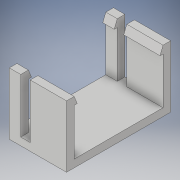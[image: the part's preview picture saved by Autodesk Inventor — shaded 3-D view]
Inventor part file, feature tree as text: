
AUTODESK INVENTOR PART (.ipt)
format: ipt  version: 2019 (Build 230136000, 136)  size: 148,480 bytes
history: native  units: mm
features: extrude x4, sketch x3, projected_geometry x1
ambient origin geometry x8: Origin, YZ Plane, XZ Plane, XY Plane, X Axis, Y Axis, Z Axis, Center Point
bodies: Solid1 (feature_tree)
feature tree (8):
  sketch  "Sketch1"  dims[d0=27.3mm d1=15.0mm]
  extrude  "Extrusion1"  Depth=15.0mm
  extrude  "Extrusion2"  Depth=2.5mm
  extrude  "Extrusion3"  Depth=2.0mm
  extrude  "Extrusion4"  Depth=2.0mm
  sketch  "Sketch2"  dims[d2=3.0mm d3=2.5mm]
  sketch  "Sketch3"  dims[d4=2.0mm d5=2.0mm d6=2.0mm d7=2.0mm d8=2.0mm d9=0.0mm d10=14.2mm d11=0.0mm d12=2.0mm d13=2.0mm d14=0.8mm d15=0.8mm d16=12.2mm d17=0.0mm d18=12.2mm d19=0.0mm]
  projected_geometry  "Projected Loop1"
